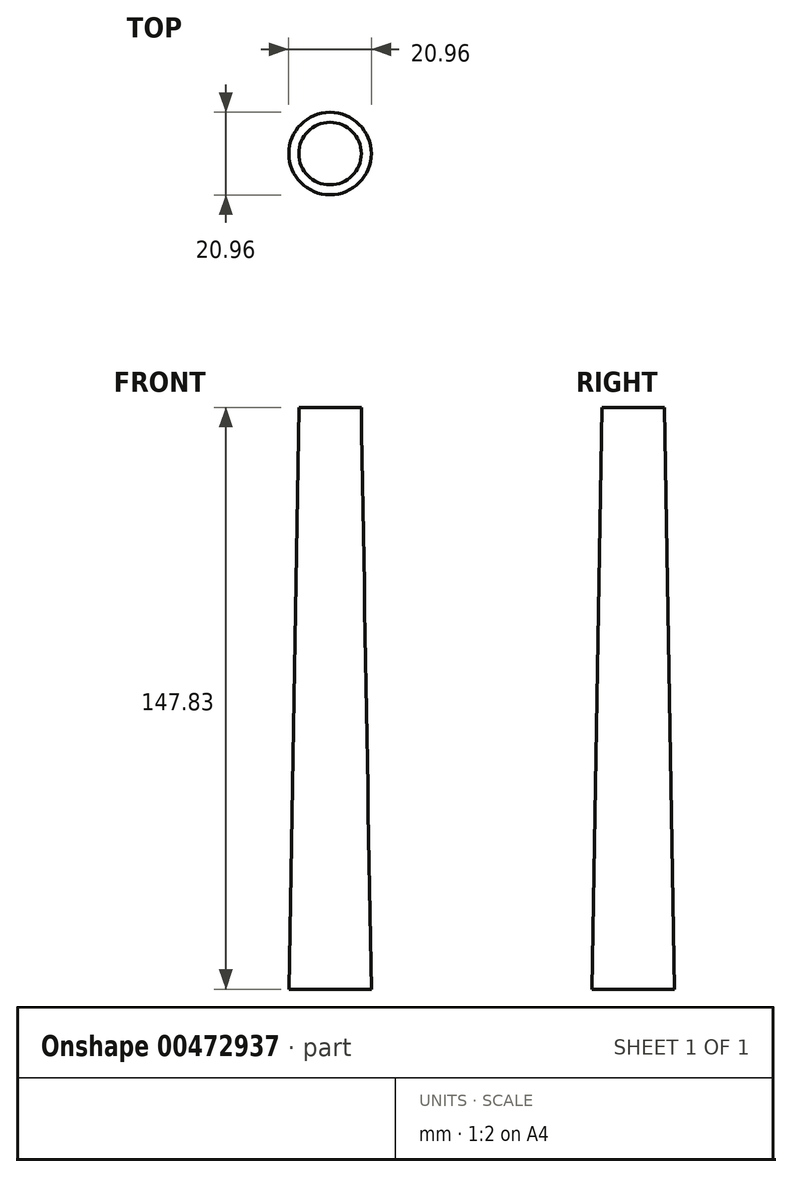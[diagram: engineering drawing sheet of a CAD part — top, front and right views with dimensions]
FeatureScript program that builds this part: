
annotation { "Feature Type Name" : "Feature", "Feature Type Description" : "" }
export const myFeature = defineFeature(function(context is Context, id is Id, definition is map)
    precondition{}
    {
        {
            var Q0;
            Q0=qCreatedBy(makeId("Top.planeOp"),FACE);
            var sketch = newSketch(context, id + "F0", { "sketchPlane" : qUnion([Q0])});
            skCircle(sketch, "E0", {"center": v(0, 0) * mm, "radius": 10.48 * mm});
            skSolve(sketch);
        }
        {
            var Q0;
            Q0=qCreatedBy(makeId("Top.planeOp"),FACE);
            cPlane(context, id + "F1", {"entities" : qUnion([Q0]), "cplaneType" : CPlaneType.OFFSET, "offset" : 147.83 * mm, "width" : 152.4 * mm, "height" : 152.4 * mm});
        }
        {
            var Q0;
            Q0=qCreatedBy(id+"F1.planeOp",FACE);
            var sketch = newSketch(context, id + "F2", { "sketchPlane" : qUnion([Q0])});
            skCircle(sketch, "E1", {"center": v(0, 0) * mm, "radius": 7.94 * mm});
            skSolve(sketch);
        }
        {
            var Q0;
            Q0 = qSketchRegion(id + "F0", true);
            var Q1;
            Q1 = qSketchRegion(id + "F2", true);
            loft(context, id + "F3", {"sheetProfilesArray" : [{ "sheetProfileEntities" : qUnion([Q0]) }, { "sheetProfileEntities" : qUnion([Q1]) }]});
        }
    });
